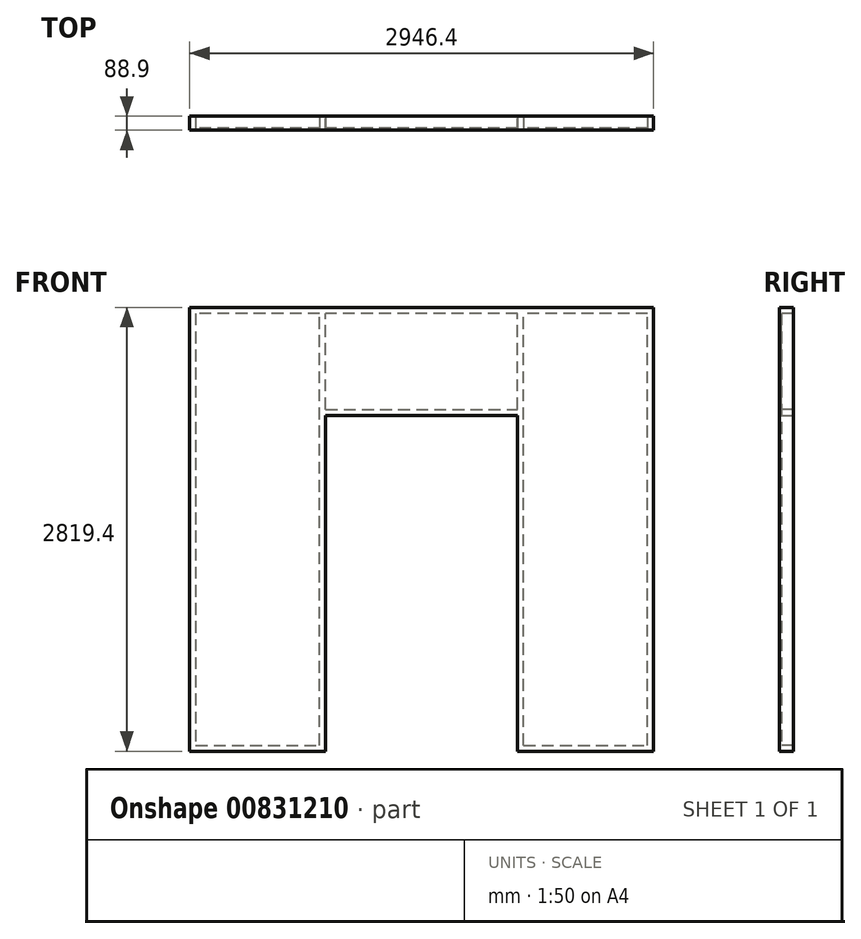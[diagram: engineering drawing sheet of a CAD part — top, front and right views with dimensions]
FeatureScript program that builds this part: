
annotation { "Feature Type Name" : "Feature", "Feature Type Description" : "" }
export const myFeature = defineFeature(function(context is Context, id is Id, definition is map)
    precondition{}
    {
        {
            var Q0;
            Q0=qCreatedBy(makeId("Front.planeOp"),FACE);
            var sketch = newSketch(context, id + "F0", { "sketchPlane" : qUnion([Q0])});
            skLineSegment(sketch, "E0.bottom", {"start": v(1473.2, 1409.7) * mm, "end": v(-1473.2, 1409.7) * mm});
            skLineSegment(sketch, "E0.top", {"start": v(1473.2, -1409.7) * mm, "end": v(609.6, -1409.7) * mm});
            skLineSegment(sketch, "E0.left", {"start": v(1473.2, 1409.7) * mm, "end": v(1473.2, -1409.7) * mm});
            skLineSegment(sketch, "E0.right", {"start": v(-1473.2, 1409.7) * mm, "end": v(-1473.2, -1409.7) * mm});
            skPoint(sketch, "E0.middle", {"position": v(0, 0) * mm});
            skLineSegment(sketch, "E1.top", {"start": v(-609.6, 723.9) * mm, "end": v(609.6, 723.9) * mm});
            skLineSegment(sketch, "E1.left", {"start": v(-609.6, -1409.7) * mm, "end": v(-609.6, 723.9) * mm});
            skLineSegment(sketch, "E1.right", {"start": v(609.6, -1409.7) * mm, "end": v(609.6, 723.9) * mm});
            skLineSegment(sketch, "E2.trimOffspring", {"start": v(-609.6, -1409.7) * mm, "end": v(-1473.2, -1409.7) * mm});
            skSolve(sketch);
        }
        {
            var Q0;
            Q0 = qSketchRegion(id + "F0", true);
            extrude(context, id + "F1", {"entities" : qUnion([Q0]), "depth" : 12.7 * mm, "offsetDistance" : 25.4 * mm});
        }
        {
            var Q0;
            Q0=makeQuery(id+"F1.opExtrude","CAP_FACE",FACE,{"disambiguationData":[OSD([sQuery(id+"F0.wireOp",EDGE,"E0.bottom"),sQuery(id+"F0.wireOp",EDGE,"E0.top"),sQuery(id+"F0.wireOp",EDGE,"E0.left"),sQuery(id+"F0.wireOp",EDGE,"E0.right"),sQuery(id+"F0.wireOp",EDGE,"E1.top"),sQuery(id+"F0.wireOp",EDGE,"E1.left"),sQuery(id+"F0.wireOp",EDGE,"E1.right"),sQuery(id+"F0.wireOp",EDGE,"E2.trimOffspring")])],"isStart":true});
            var sketch = newSketch(context, id + "F2", { "sketchPlane" : qUnion([Q0])});
            skLineSegment(sketch, "E3.bottom", {"start": v(-1473.2, 1409.7) * mm, "end": v(1473.2, 1409.7) * mm});
            skLineSegment(sketch, "E3.top", {"start": v(-1473.2, 1371.6) * mm, "end": v(1473.2, 1371.6) * mm});
            skLineSegment(sketch, "E3.left", {"start": v(-1473.2, 1409.7) * mm, "end": v(-1473.2, 1371.6) * mm});
            skLineSegment(sketch, "E3.right", {"start": v(1473.2, 1409.7) * mm, "end": v(1473.2, 1371.6) * mm});
            skLineSegment(sketch, "E4.bottom", {"start": v(1473.2, 1371.6) * mm, "end": v(1435.1, 1371.6) * mm});
            skLineSegment(sketch, "E4.top", {"start": v(1473.2, -1371.6) * mm, "end": v(1435.1, -1371.6) * mm});
            skLineSegment(sketch, "E4.left", {"start": v(1473.2, 1371.6) * mm, "end": v(1473.2, -1371.6) * mm});
            skLineSegment(sketch, "E4.right", {"start": v(1435.1, 1371.6) * mm, "end": v(1435.1, -1371.6) * mm});
            skLineSegment(sketch, "E5.bottom", {"start": v(1473.2, -1371.6) * mm, "end": v(609.6, -1371.6) * mm});
            skLineSegment(sketch, "E5.top", {"start": v(1473.2, -1409.7) * mm, "end": v(609.6, -1409.7) * mm});
            skLineSegment(sketch, "E5.left", {"start": v(1473.2, -1371.6) * mm, "end": v(1473.2, -1409.7) * mm});
            skLineSegment(sketch, "E5.right", {"start": v(609.6, -1371.6) * mm, "end": v(609.6, -1409.7) * mm});
            skLineSegment(sketch, "E6.bottom", {"start": v(609.6, -1371.6) * mm, "end": v(647.7, -1371.6) * mm});
            skLineSegment(sketch, "E6.top", {"start": v(609.6, 1371.6) * mm, "end": v(647.7, 1371.6) * mm});
            skLineSegment(sketch, "E6.left", {"start": v(609.6, -1371.6) * mm, "end": v(609.6, 1371.6) * mm});
            skLineSegment(sketch, "E6.right", {"start": v(647.7, -1371.6) * mm, "end": v(647.7, 1371.6) * mm});
            skLineSegment(sketch, "E7.bottom", {"start": v(609.6, 762) * mm, "end": v(-609.6, 762) * mm});
            skLineSegment(sketch, "E7.top", {"start": v(609.6, 723.9) * mm, "end": v(-609.6, 723.9) * mm});
            skLineSegment(sketch, "E7.left", {"start": v(609.6, 762) * mm, "end": v(609.6, 723.9) * mm});
            skLineSegment(sketch, "E7.right", {"start": v(-609.6, 762) * mm, "end": v(-609.6, 723.9) * mm});
            skLineSegment(sketch, "E8.bottom", {"start": v(-609.6, -1409.7) * mm, "end": v(-1473.2, -1409.7) * mm});
            skLineSegment(sketch, "E8.top", {"start": v(-609.6, -1371.6) * mm, "end": v(-1473.2, -1371.6) * mm});
            skLineSegment(sketch, "E8.left", {"start": v(-609.6, -1409.7) * mm, "end": v(-609.6, -1371.6) * mm});
            skLineSegment(sketch, "E8.right", {"start": v(-1473.2, -1409.7) * mm, "end": v(-1473.2, -1371.6) * mm});
            skLineSegment(sketch, "E9.bottom", {"start": v(-1473.2, -1371.6) * mm, "end": v(-1435.1, -1371.6) * mm});
            skLineSegment(sketch, "E9.top", {"start": v(-1473.2, 1371.6) * mm, "end": v(-1435.1, 1371.6) * mm});
            skLineSegment(sketch, "E9.left", {"start": v(-1473.2, -1371.6) * mm, "end": v(-1473.2, 1371.6) * mm});
            skLineSegment(sketch, "E9.right", {"start": v(-1435.1, -1371.6) * mm, "end": v(-1435.1, 1371.6) * mm});
            skLineSegment(sketch, "E10.bottom", {"start": v(-1079.5, 1371.6) * mm, "end": v(-1041.4, 1371.6) * mm});
            skLineSegment(sketch, "E10.top", {"start": v(-1079.5, -1371.6) * mm, "end": v(-1041.4, -1371.6) * mm});
            skLineSegment(sketch, "E10.left", {"start": v(-1079.5, 1371.6) * mm, "end": v(-1079.5, -1371.6) * mm});
            skLineSegment(sketch, "E10.right", {"start": v(-1041.4, 1371.6) * mm, "end": v(-1041.4, -1371.6) * mm});
            skLineSegment(sketch, "E11.bottom", {"start": v(-609.6, -1371.6) * mm, "end": v(-647.7, -1371.6) * mm});
            skLineSegment(sketch, "E11.top", {"start": v(-609.6, 1371.6) * mm, "end": v(-647.7, 1371.6) * mm});
            skLineSegment(sketch, "E11.left", {"start": v(-609.6, -1371.6) * mm, "end": v(-609.6, 1371.6) * mm});
            skLineSegment(sketch, "E11.right", {"start": v(-647.7, -1371.6) * mm, "end": v(-647.7, 1371.6) * mm});
            skLineSegment(sketch, "E12.bottom", {"start": v(1041.4, 1371.6) * mm, "end": v(1079.5, 1371.6) * mm});
            skLineSegment(sketch, "E12.top", {"start": v(1041.4, -1371.6) * mm, "end": v(1079.5, -1371.6) * mm});
            skLineSegment(sketch, "E12.left", {"start": v(1041.4, 1371.6) * mm, "end": v(1041.4, -1371.6) * mm});
            skLineSegment(sketch, "E12.right", {"start": v(1079.5, 1371.6) * mm, "end": v(1079.5, -1371.6) * mm});
            skLineSegment(sketch, "E13.bottom", {"start": v(-38.1, 1371.6) * mm, "end": v(0, 1371.6) * mm});
            skLineSegment(sketch, "E13.top", {"start": v(-38.1, 762) * mm, "end": v(0, 762) * mm});
            skLineSegment(sketch, "E13.left", {"start": v(-38.1, 1371.6) * mm, "end": v(-38.1, 762) * mm});
            skLineSegment(sketch, "E13.right", {"start": v(0, 1371.6) * mm, "end": v(0, 762) * mm});
            skSolve(sketch);
        }
        {
            var Q0;
            Q0 = qSketchRegion(id + "F2", true);
            var Q1;
            Q1=makeQuery(id+"F2.imprint","IMPRINT",FACE,{"disambiguationData":[TD([[makeQuery(id+"F2.imprint","IMPRINT",EDGE,{"derivedFrom":sQuery(id+"F2.wireOp",EDGE,"E10.bottom")}),-1.0]])]});
            var Q2;
            Q2=makeQuery(id+"F2.imprint","IMPRINT",FACE,{"disambiguationData":[TD([[makeQuery(id+"F2.imprint","IMPRINT",EDGE,{"derivedFrom":sQuery(id+"F2.wireOp",EDGE,"E12.bottom")}),-1.0]])]});
            var Q3;
            Q3=makeQuery(id+"F2.imprint","IMPRINT",FACE,{"disambiguationData":[TD([[makeQuery(id+"F2.imprint","IMPRINT",EDGE,{"derivedFrom":sQuery(id+"F2.wireOp",EDGE,"E13.bottom")}),-1.0]])]});
            extrude(context, id + "F3", {"entities" : qUnion([Q0, Q1, Q2, Q3]), "operationType" : NewBodyOperationType.ADD, "depth" : 76.2 * mm, "offsetDistance" : 25.4 * mm});
        }
    });
